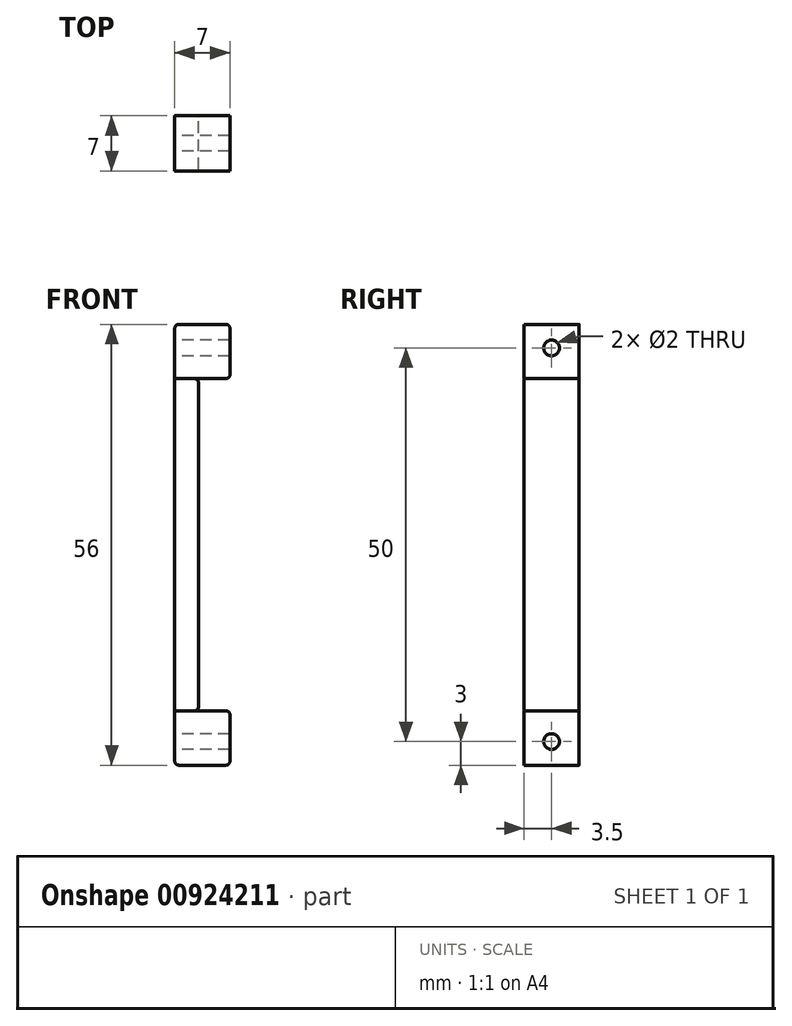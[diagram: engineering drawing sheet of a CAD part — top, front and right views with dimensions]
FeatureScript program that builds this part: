
annotation { "Feature Type Name" : "Feature", "Feature Type Description" : "" }
export const myFeature = defineFeature(function(context is Context, id is Id, definition is map)
    precondition{}
    {
        {
            var Q0;
            Q0=qCreatedBy(makeId("Right.planeOp"),FACE);
            var sketch = newSketch(context, id + "F0", { "sketchPlane" : qUnion([Q0])});
            skLineSegment(sketch, "E0.top", {"start": v(3.5, 28) * mm, "end": v(-3.5, 28) * mm});
            skLineSegment(sketch, "E0.left", {"start": v(3.5, 22.5) * mm, "end": v(3.5, 28) * mm});
            skLineSegment(sketch, "E0.right", {"start": v(-3.5, 22.5) * mm, "end": v(-3.5, 28) * mm});
            skCircle(sketch, "E1", {"center": v(0, 25) * mm, "radius": 1 * mm});
            skPoint(sketch, "E1.centerSnap0", {"position": v(3.5, 25.25) * mm});
            skPoint(sketch, "E1.centerSnap1", {"position": v(0, 28) * mm});
            skPoint(sketch, "E2.MirrorP", {"position": v(-0.5, -26.95) * mm});
            skLineSegment(sketch, "E3.MirrorCS", {"start": v(-3.5, -22.5) * mm, "end": v(-3.5, -28) * mm});
            skPoint(sketch, "E4.MirrorP", {"position": v(3, -24.72) * mm});
            skCircle(sketch, "E5.MirrorC", {"center": v(0, -25) * mm, "radius": 1 * mm});
            skLineSegment(sketch, "E6.MirrorCS", {"start": v(3.5, -22.5) * mm, "end": v(3.5, -28) * mm});
            skLineSegment(sketch, "E7.MirrorCS", {"start": v(3.5, -28) * mm, "end": v(-3.5, -28) * mm});
            skLineSegment(sketch, "E8", {"start": v(-3.5, -22.5) * mm, "end": v(-3.5, 22.5) * mm});
            skLineSegment(sketch, "E9", {"start": v(3.5, 22.5) * mm, "end": v(3.5, -22.5) * mm});
            skLineSegment(sketch, "E10", {"start": v(-3.5, -21.1) * mm, "end": v(3.5, -21.1) * mm});
            skLineSegment(sketch, "E11", {"start": v(-3.5, 21.1) * mm, "end": v(3.5, 21.1) * mm});
            skSolve(sketch);
        }
        {
            var Q0;
            {var subQ1=sQuery(id+"F0.wireOp",EDGE,"E3.MirrorCS");Q0=makeQuery(id+"F0.imprint","IMPRINT",FACE,{"disambiguationData":[TD([[makeQuery(id+"F0.imprint","IMPRINT",EDGE,{"derivedFrom":subQ1}),1.0]])]});}
            var Q1;
            Q1=makeQuery(id+"F0.imprint","IMPRINT",FACE,{"disambiguationData":[TD([[makeQuery(id+"F0.imprint","IMPRINT",EDGE,{"derivedFrom":sQuery(id+"F0.wireOp",EDGE,"E0.top")}),1.0]])]});
            extrude(context, id + "F1", {"entities" : qUnion([Q0, Q1]), "depth" : 7 * mm, "offsetDistance" : 25 * mm});
        }
        {
            var Q0;
            {var subQ0=sQuery(id+"F0.wireOp",EDGE,"E10");Q0=makeQuery(id+"F0.imprint","IMPRINT",FACE,{"disambiguationData":[TD([[makeQuery(id+"F0.imprint","IMPRINT",EDGE,{"derivedFrom":subQ0}),1.0]])]});}
            extrude(context, id + "F2", {"entities" : qUnion([Q0]), "depth" : 3 * mm, "offsetDistance" : 25 * mm});
        }
        {
            var Q0;
            Q0=makeQuery(id+"F1.opExtrude","CAP_EDGE",EDGE,{"disambiguationData":[OSD([sQuery(id+"F0.wireOp",EDGE,"E10")])],"isStart":false});
            var Q1;
            Q1=makeQuery(id+"F1.opExtrude","CAP_EDGE",EDGE,{"disambiguationData":[OSD([sQuery(id+"F0.wireOp",EDGE,"E7.MirrorCS")])],"isStart":false});
            var Q2;
            Q2=makeQuery(id+"F1.opExtrude","CAP_EDGE",EDGE,{"disambiguationData":[OSD([sQuery(id+"F0.wireOp",EDGE,"E11")])],"isStart":false});
            var Q3;
            Q3=makeQuery(id+"F1.opExtrude","CAP_EDGE",EDGE,{"disambiguationData":[OSD([sQuery(id+"F0.wireOp",EDGE,"E0.top")])],"isStart":false});
            var Q4;
            Q4=makeQuery(id+"F1.opExtrude","CAP_EDGE",EDGE,{"disambiguationData":[OSD([sQuery(id+"F0.wireOp",EDGE,"E0.top")])],"isStart":true});
            var Q5;
            Q5=makeQuery(id+"F1.opExtrude","CAP_EDGE",EDGE,{"disambiguationData":[OSD([sQuery(id+"F0.wireOp",EDGE,"E7.MirrorCS")])],"isStart":true});
            var Q6;
            Q6=makeQuery(id+"F2.opExtrude","CAP_EDGE",EDGE,{"disambiguationData":[OSD([sQuery(id+"F0.wireOp",EDGE,"E11")])],"isStart":false});
            var Q7;
            Q7=makeQuery(id+"F2.opExtrude","CAP_EDGE",EDGE,{"disambiguationData":[OSD([sQuery(id+"F0.wireOp",EDGE,"E10")])],"isStart":false});
            fillet(context, id + "F3", {"entities" : qUnion([Q0, Q1, Q2, Q3, Q4, Q5, Q6, Q7]), "radius" : 0.5 * mm, "tangentPropagation" : true, "allowEdgeOverflow" : false});
        }
        {
            var Q0;
            Q0=makeQuery(id+"F2.opExtrude","CAP_EDGE",EDGE,{"disambiguationData":[OSD([sQuery(id+"F0.wireOp",EDGE,"E9")])],"isStart":false});
            var Q1;
            Q1=makeQuery(id+"F2.opExtrude","CAP_EDGE",EDGE,{"disambiguationData":[OSD([sQuery(id+"F0.wireOp",EDGE,"E8")])],"isStart":false});
            fillet(context, id + "F4", {"entities" : qUnion([Q0, Q1]), "radius" : 0.2 * mm, "tangentPropagation" : true, "allowEdgeOverflow" : false});
        }
    });
